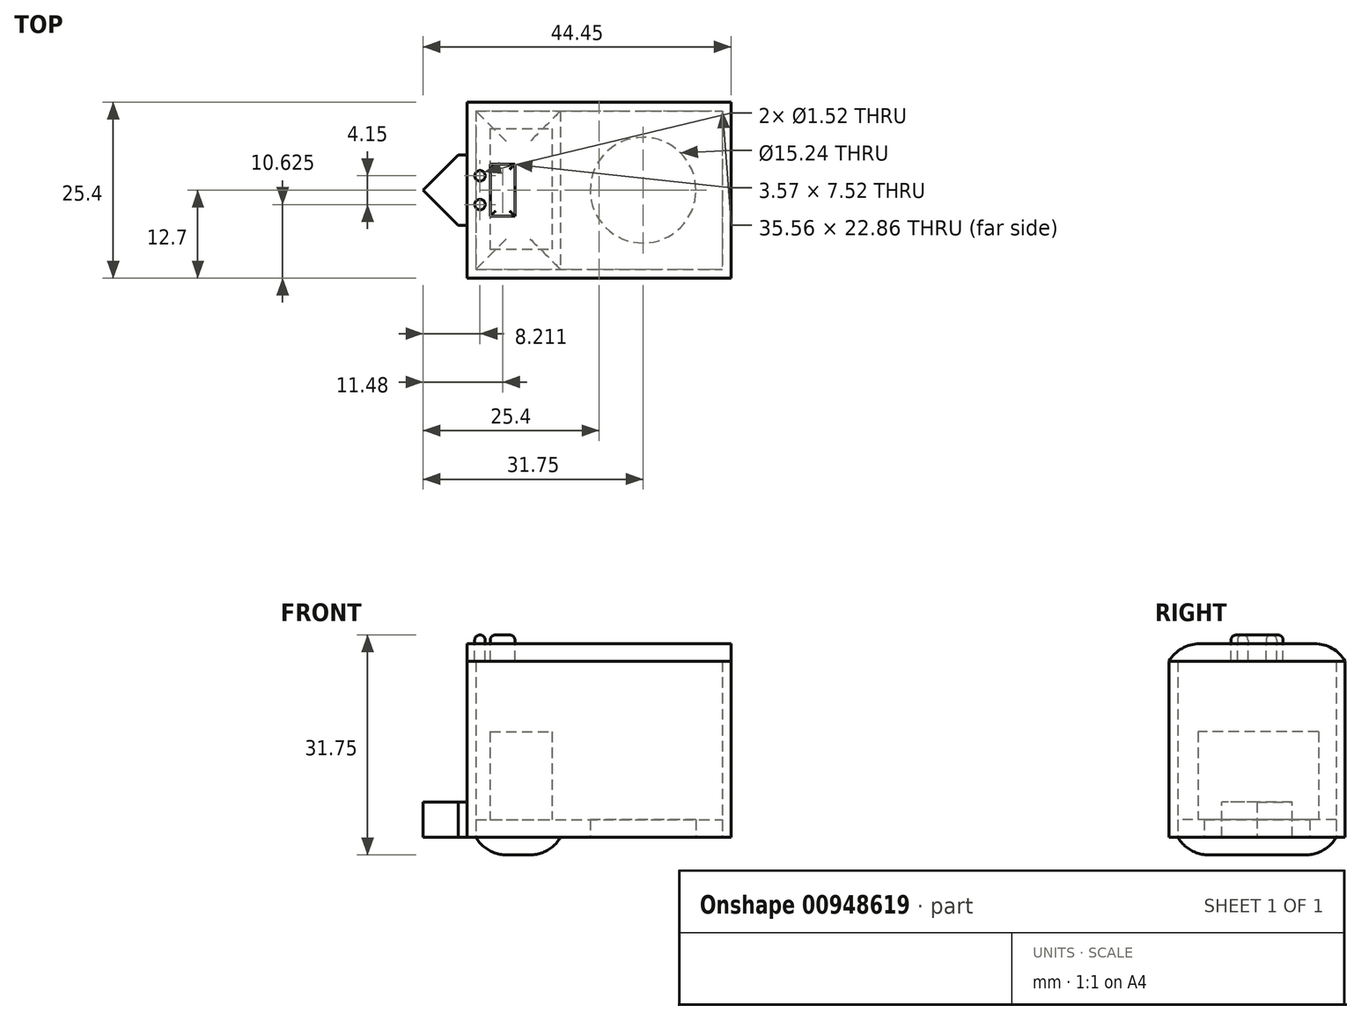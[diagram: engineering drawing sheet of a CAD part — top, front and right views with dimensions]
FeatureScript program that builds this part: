
annotation { "Feature Type Name" : "Feature", "Feature Type Description" : "" }
export const myFeature = defineFeature(function(context is Context, id is Id, definition is map)
    precondition{}
    {
        {
            var Q0;
            Q0=qCreatedBy(makeId("Top.planeOp"),FACE);
            var sketch = newSketch(context, id + "F0", { "sketchPlane" : qUnion([Q0])});
            skLineSegment(sketch, "E0.bottom", {"start": v(19.05, 12.7) * mm, "end": v(-19.05, 12.7) * mm});
            skLineSegment(sketch, "E0.top", {"start": v(19.05, -12.7) * mm, "end": v(-19.05, -12.7) * mm});
            skLineSegment(sketch, "E0.left", {"start": v(19.05, 12.7) * mm, "end": v(19.05, -12.7) * mm});
            skLineSegment(sketch, "E0.right", {"start": v(-19.05, 12.7) * mm, "end": v(-19.05, -12.7) * mm});
            skPoint(sketch, "E0.middle", {"position": v(0, 0) * mm});
            skLineSegment(sketch, "E1.bottom", {"start": v(-17.78, 11.43) * mm, "end": v(17.78, 11.43) * mm});
            skLineSegment(sketch, "E1.top", {"start": v(-17.78, -11.43) * mm, "end": v(17.78, -11.43) * mm});
            skLineSegment(sketch, "E1.left", {"start": v(-17.78, 11.43) * mm, "end": v(-17.78, -11.43) * mm});
            skLineSegment(sketch, "E1.right", {"start": v(17.78, 11.43) * mm, "end": v(17.78, -11.43) * mm});
            skCircle(sketch, "E2", {"center": v(6.35, 0) * mm, "radius": 7.62 * mm});
            skPoint(sketch, "E3.start.orphan", {"position": v(17.78, 0) * mm});
            skPoint(sketch, "E4.start.orphan", {"position": v(-17.78, 0) * mm});
            skLineSegment(sketch, "E5", {"start": v(-5.55, 11.43) * mm, "end": v(-5.55, -11.43) * mm});
            skSolve(sketch);
        }
        {
            var Q0;
            Q0 = qSketchRegion(id + "F0", true);
            extrude(context, id + "F1", {"entities" : qUnion([Q0]), "depth" : 25.4 * mm, "offsetDistance" : 25.4 * mm});
        }
        {
            var Q0;
            {var subQ0=sQuery(id+"F0.wireOp",EDGE,"E1.left");Q0=makeQuery(id+"F0.imprint","IMPRINT",FACE,{"disambiguationData":[TD([[makeQuery(id+"F0.imprint","IMPRINT",EDGE,{"derivedFrom":subQ0}),1.0]])]});}
            extrude(context, id + "F2", {"entities" : qUnion([Q0]), "oppositeDirection" : true, "depth" : 2.54 * mm, "offsetDistance" : 25.4 * mm});
        }
        {
            var Q0;
            {var subQ0=sQuery(id+"F0.wireOp",EDGE,"E1.right");Q0=makeQuery(id+"F0.imprint","IMPRINT",FACE,{"disambiguationData":[TD([[makeQuery(id+"F0.imprint","IMPRINT",EDGE,{"derivedFrom":subQ0}),-1.0]])]});}
            var Q1;
            {var subQ0=sQuery(id+"F0.wireOp",EDGE,"E1.left");Q1=makeQuery(id+"F0.imprint","IMPRINT",FACE,{"disambiguationData":[TD([[makeQuery(id+"F0.imprint","IMPRINT",EDGE,{"derivedFrom":subQ0}),1.0]])]});}
            extrude(context, id + "F3", {"entities" : qUnion([Q0, Q1]), "depth" : 2.54 * mm, "offsetDistance" : 25.4 * mm});
        }
        {
            var Q0;
            Q0=makeQuery(id+"F1.opExtrude","CAP_FACE",FACE,{"disambiguationData":[OSD([sQuery(id+"F0.wireOp",EDGE,"E0.bottom"),sQuery(id+"F0.wireOp",EDGE,"E0.top"),sQuery(id+"F0.wireOp",EDGE,"E0.left"),sQuery(id+"F0.wireOp",EDGE,"E0.right"),sQuery(id+"F0.wireOp",EDGE,"E1.bottom"),sQuery(id+"F0.wireOp",EDGE,"E1.top"),sQuery(id+"F0.wireOp",EDGE,"E1.left"),sQuery(id+"F0.wireOp",EDGE,"E1.right")])],"isStart":false});
            var sketch = newSketch(context, id + "F4", { "sketchPlane" : qUnion([Q0])});
            skLineSegment(sketch, "E6.bottom", {"start": v(-19.05, 12.7) * mm, "end": v(19.05, 12.7) * mm});
            skLineSegment(sketch, "E6.top", {"start": v(-19.05, -12.7) * mm, "end": v(19.05, -12.7) * mm});
            skLineSegment(sketch, "E6.left", {"start": v(-19.05, 12.7) * mm, "end": v(-19.05, -12.7) * mm});
            skLineSegment(sketch, "E6.right", {"start": v(19.05, 12.7) * mm, "end": v(19.05, -12.7) * mm});
            skSolve(sketch);
        }
        {
            var Q0;
            Q0 = qSketchRegion(id + "F4", true);
            extrude(context, id + "F5", {"entities" : qUnion([Q0]), "depth" : 2.54 * mm, "offsetDistance" : 25.4 * mm});
        }
        {
            var Q0;
            Q0=makeQuery(id+"F2.opExtrude","CAP_EDGE",EDGE,{"disambiguationData":[OSD([sQuery(id+"F0.wireOp",EDGE,"E1.left")])],"isStart":false});
            var Q1;
            Q1=makeQuery(id+"F2.opExtrude","CAP_EDGE",EDGE,{"disambiguationData":[OSD([sQuery(id+"F0.wireOp",EDGE,"E1.top")])],"isStart":false});
            var Q2;
            Q2=makeQuery(id+"F2.opExtrude","CAP_EDGE",EDGE,{"disambiguationData":[OSD([sQuery(id+"F0.wireOp",EDGE,"E5")])],"isStart":false});
            var Q3;
            Q3=makeQuery(id+"F2.opExtrude","CAP_EDGE",EDGE,{"disambiguationData":[OSD([sQuery(id+"F0.wireOp",EDGE,"E1.bottom")])],"isStart":false});
            fillet(context, id + "F6", {"entities" : qUnion([Q0, Q1, Q2, Q3]), "radius" : 5.08 * mm, "tangentPropagation" : true, "allowEdgeOverflow" : false});
        }
        {
            var Q0;
            Q0=makeQuery(id+"F5.opExtrude","CAP_EDGE",EDGE,{"disambiguationData":[OSD([sQuery(id+"F4.wireOp",EDGE,"E6.bottom")])],"isStart":false});
            var Q1;
            Q1=makeQuery(id+"F5.opExtrude","CAP_EDGE",EDGE,{"disambiguationData":[OSD([sQuery(id+"F4.wireOp",EDGE,"E6.top")])],"isStart":false});
            fillet(context, id + "F7", {"entities" : qUnion([Q0, Q1]), "radius" : 5.08 * mm, "tangentPropagation" : true, "allowEdgeOverflow" : false});
        }
        {
            var Q0;
            Q0=makeQuery(id+"F1.opExtrude","SWEPT_FACE",FACE,{"disambiguationData":[OSD([sQuery(id+"F0.wireOp",EDGE,"E0.right")])]});
            var sketch = newSketch(context, id + "F8", { "sketchPlane" : qUnion([Q0])});
            skLineSegment(sketch, "E7", {"start": v(0, 0) * mm, "end": v(-5.08, 0) * mm});
            skLineSegment(sketch, "E8", {"start": v(-5.08, 0) * mm, "end": v(-5.08, 5.08) * mm});
            skLineSegment(sketch, "E9", {"start": v(-5.08, 5.08) * mm, "end": v(0, 5.08) * mm});
            skLineSegment(sketch, "E10", {"start": v(0, 5.08) * mm, "end": v(5.08, 5.08) * mm});
            skLineSegment(sketch, "E11", {"start": v(5.08, 0) * mm, "end": v(0, 0) * mm});
            skLineSegment(sketch, "E12", {"start": v(5.08, 0) * mm, "end": v(5.08, 5.08) * mm});
            skSolve(sketch);
        }
        {
            var Q0;
            Q0=makeQuery(id+"F8.imprint","IMPRINT",FACE,{"disambiguationData":[TD([[makeQuery(id+"F8.imprint","IMPRINT",EDGE,{"derivedFrom":sQuery(id+"F8.wireOp",EDGE,"E7")}),1.0]])]});
            extrude(context, id + "F9", {"entities" : qUnion([Q0]), "operationType" : NewBodyOperationType.ADD, "depth" : 6.35 * mm, "offsetDistance" : 25.4 * mm});
        }
        {
            var Q0;
            Q0=makeQuery(id+"F9.opExtrude","CAP_EDGE",EDGE,{"disambiguationData":[OSD([sQuery(id+"F8.wireOp",EDGE,"E12")])],"isStart":false});
            var Q1;
            Q1=makeQuery(id+"F9.opExtrude","CAP_EDGE",EDGE,{"disambiguationData":[OSD([sQuery(id+"F8.wireOp",EDGE,"E8")])],"isStart":false});
            chamfer(context, id + "F10", {"entities" : qUnion([Q0, Q1]), "width" : 5.08 * mm, "tangentPropagation" : true});
        }
        {
            var Q0;
            Q0=makeQuery(id+"F3.opExtrude","CAP_FACE",FACE,{"disambiguationData":[OSD([sQuery(id+"F0.wireOp",EDGE,"E1.bottom"),sQuery(id+"F0.wireOp",EDGE,"E1.top"),sQuery(id+"F0.wireOp",EDGE,"E1.left"),sQuery(id+"F0.wireOp",EDGE,"E1.right"),sQuery(id+"F0.wireOp",EDGE,"E2")])],"isStart":false});
            var sketch = newSketch(context, id + "F11", { "sketchPlane" : qUnion([Q0])});
            skLineSegment(sketch, "E13.bottom", {"start": v(-15.72, 8.88) * mm, "end": v(-6.78, 8.88) * mm});
            skLineSegment(sketch, "E13.top", {"start": v(-15.72, -8.52) * mm, "end": v(-6.78, -8.52) * mm});
            skLineSegment(sketch, "E13.left", {"start": v(-15.72, 8.88) * mm, "end": v(-15.72, -8.52) * mm});
            skLineSegment(sketch, "E13.right", {"start": v(-6.78, 8.88) * mm, "end": v(-6.78, -8.52) * mm});
            skSolve(sketch);
        }
        {
            var Q0;
            Q0 = qSketchRegion(id + "F11", true);
            extrude(context, id + "F12", {"entities" : qUnion([Q0]), "depth" : 12.7 * mm, "offsetDistance" : 25.4 * mm});
        }
        {
            var Q0;
            Q0=makeQuery(id+"F5.opExtrude","CAP_FACE",FACE,{"disambiguationData":[OSD([sQuery(id+"F4.wireOp",EDGE,"E6.bottom"),sQuery(id+"F4.wireOp",EDGE,"E6.top"),sQuery(id+"F4.wireOp",EDGE,"E6.left"),sQuery(id+"F4.wireOp",EDGE,"E6.right")])],"isStart":false});
            var sketch = newSketch(context, id + "F13", { "sketchPlane" : qUnion([Q0])});
            skCircle(sketch, "E14", {"center": v(-17.19, 2.08) * mm, "radius": 0.76 * mm});
            skCircle(sketch, "E15", {"center": v(-17.19, -2.08) * mm, "radius": 0.76 * mm});
            skLineSegment(sketch, "E16.bottom", {"start": v(-15.7, 3.76) * mm, "end": v(-12.13, 3.76) * mm});
            skLineSegment(sketch, "E16.top", {"start": v(-15.7, -3.76) * mm, "end": v(-12.13, -3.76) * mm});
            skLineSegment(sketch, "E16.left", {"start": v(-15.7, 3.76) * mm, "end": v(-15.7, -3.76) * mm});
            skLineSegment(sketch, "E16.right", {"start": v(-12.13, 3.76) * mm, "end": v(-12.13, -3.76) * mm});
            skPoint(sketch, "E16.middle", {"position": v(-13.92, 0) * mm});
            skPoint(sketch, "E17.orphan", {"position": v(-17.19, 8.3) * mm});
            skPoint(sketch, "E18.orphan", {"position": v(-17.19, 4.15) * mm});
            skPoint(sketch, "E19.orphan", {"position": v(-17.19, 0) * mm});
            skPoint(sketch, "E20.end.orphan", {"position": v(-17.19, -4.15) * mm});
            skPoint(sketch, "E21.trimOffspring.end.orphan", {"position": v(-17.19, -8.3) * mm});
            skSolve(sketch);
        }
        {
            var Q0;
            Q0 = qSketchRegion(id + "F13", true);
            var Q1;
            Q1=makeQuery(id+"F5.opExtrude","CAP_FACE",FACE,{"disambiguationData":[OSD([sQuery(id+"F4.wireOp",EDGE,"E6.bottom"),sQuery(id+"F4.wireOp",EDGE,"E6.top"),sQuery(id+"F4.wireOp",EDGE,"E6.left"),sQuery(id+"F4.wireOp",EDGE,"E6.right")])],"isStart":true});
            extrude(context, id + "F14", {"entities" : qUnion([Q0]), "operationType" : NewBodyOperationType.REMOVE, "endBound" : BoundingType.UP_TO_SURFACE, "oppositeDirection" : true, "depth" : 25.4 * mm, "endBoundEntityFace" : qUnion([Q1]), "offsetDistance" : 25.4 * mm});
        }
        {
            var Q0;
            Q0=makeQuery(id+"F13.imprint","IMPRINT",FACE,{"disambiguationData":[TD([[makeQuery(id+"F13.imprint","IMPRINT",EDGE,{"derivedFrom":sQuery(id+"F13.wireOp",EDGE,"E14")}),1.0]])]});
            var Q1;
            Q1=makeQuery(id+"F13.imprint","IMPRINT",FACE,{"disambiguationData":[TD([[makeQuery(id+"F13.imprint","IMPRINT",EDGE,{"derivedFrom":sQuery(id+"F13.wireOp",EDGE,"E15")}),1.0]])]});
            var Q2;
            Q2=makeQuery(id+"F13.imprint","IMPRINT",FACE,{"disambiguationData":[TD([[makeQuery(id+"F13.imprint","IMPRINT",EDGE,{"derivedFrom":sQuery(id+"F13.wireOp",EDGE,"E16.bottom")}),-1.0]])]});
            extrude(context, id + "F15", {"entities" : qUnion([Q0, Q1, Q2]), "depth" : 1.27 * mm, "offsetDistance" : 25.4 * mm});
        }
        {
            var Q0;
            Q0=makeQuery(id+"F15.opExtrude","CAP_EDGE",EDGE,{"disambiguationData":[OSD([sQuery(id+"F13.wireOp",EDGE,"E15")])],"isStart":false});
            var Q1;
            Q1=makeQuery(id+"F15.opExtrude","CAP_EDGE",EDGE,{"disambiguationData":[OSD([sQuery(id+"F13.wireOp",EDGE,"E14")])],"isStart":false});
            var Q2;
            Q2=makeQuery(id+"F15.opExtrude","CAP_EDGE",EDGE,{"disambiguationData":[OSD([sQuery(id+"F13.wireOp",EDGE,"E16.left")])],"isStart":false});
            var Q3;
            Q3=makeQuery(id+"F15.opExtrude","CAP_EDGE",EDGE,{"disambiguationData":[OSD([sQuery(id+"F13.wireOp",EDGE,"E16.top")])],"isStart":false});
            var Q4;
            Q4=makeQuery(id+"F15.opExtrude","CAP_EDGE",EDGE,{"disambiguationData":[OSD([sQuery(id+"F13.wireOp",EDGE,"E16.right")])],"isStart":false});
            var Q5;
            Q5=makeQuery(id+"F15.opExtrude","CAP_EDGE",EDGE,{"disambiguationData":[OSD([sQuery(id+"F13.wireOp",EDGE,"E16.bottom")])],"isStart":false});
            fillet(context, id + "F16", {"entities" : qUnion([Q0, Q1, Q2, Q3, Q4, Q5]), "radius" : 0.76 * mm, "tangentPropagation" : true, "allowEdgeOverflow" : false});
        }
    });
